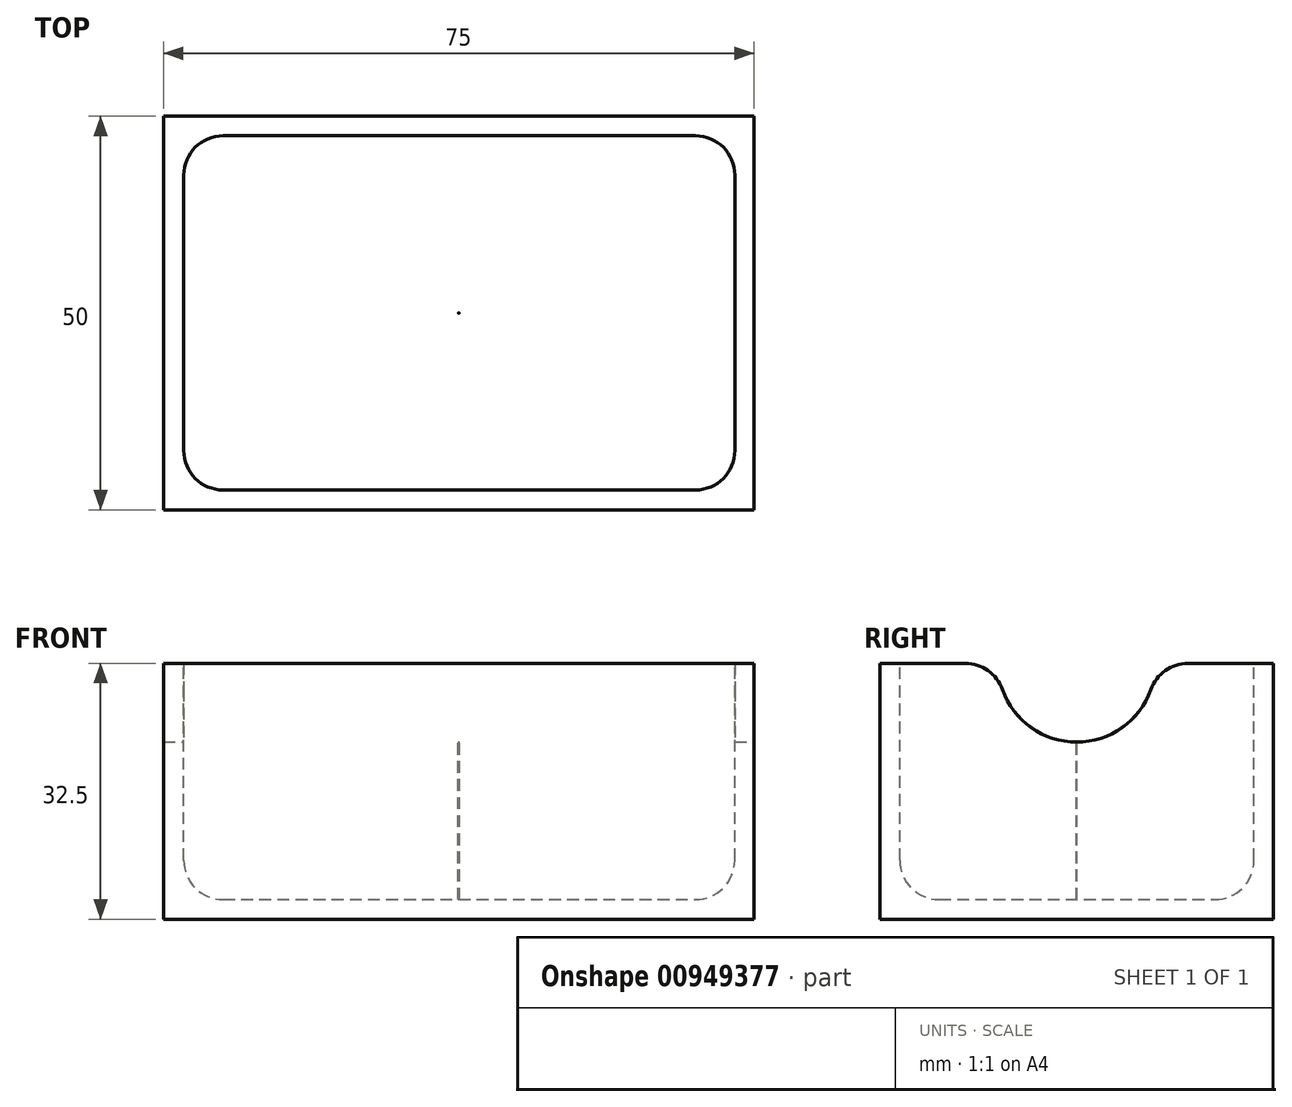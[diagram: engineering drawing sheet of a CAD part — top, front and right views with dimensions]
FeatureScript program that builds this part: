
annotation { "Feature Type Name" : "Feature", "Feature Type Description" : "" }
export const myFeature = defineFeature(function(context is Context, id is Id, definition is map)
    precondition{}
    {
        {
            assignVariable(context, id + "F0", {"name" : "Length", "anyValue" : 75});
        }
        {
            var Q0;
            Q0=qCreatedBy(makeId("Top.planeOp"),FACE);
            var sketch = newSketch(context, id + "F1", { "sketchPlane" : qUnion([Q0])});
            skLineSegment(sketch, "E0.bottom", {"start": v(37.5, -25) * mm, "end": v(-37.5, -25) * mm});
            skLineSegment(sketch, "E0.top", {"start": v(37.5, 25) * mm, "end": v(-37.5, 25) * mm});
            skLineSegment(sketch, "E0.left", {"start": v(37.5, -25) * mm, "end": v(37.5, 25) * mm});
            skLineSegment(sketch, "E0.right", {"start": v(-37.5, -25) * mm, "end": v(-37.5, 25) * mm});
            skPoint(sketch, "E0.middle", {"position": v(0, 0) * mm});
            skSolve(sketch);
        }
        {
            var Q0;
            Q0=makeQuery(id+"F1.imprint","IMPRINT",FACE,{"disambiguationData":[TD([[makeQuery(id+"F1.imprint","IMPRINT",EDGE,{"derivedFrom":sQuery(id+"F1.wireOp",EDGE,"E0.bottom")}),-1.0]])]});
            extrude(context, id + "F2", {"entities" : qUnion([Q0]), "depth" : 32.5 * mm, "offsetDistance" : 25 * mm});
        }
        {
            var Q0;
            Q0=makeQuery(id+"F2.opExtrude","CAP_FACE",FACE,{"disambiguationData":[OSD([sQuery(id+"F1.wireOp",EDGE,"E0.bottom"),sQuery(id+"F1.wireOp",EDGE,"E0.top"),sQuery(id+"F1.wireOp",EDGE,"E0.left"),sQuery(id+"F1.wireOp",EDGE,"E0.right")])],"isStart":false});
            var sketch = newSketch(context, id + "F3", { "sketchPlane" : qUnion([Q0])});
            skLineSegment(sketch, "E1.bottom", {"start": v(-0.07, 0.02) * mm, "end": v(0.07, 0.02) * mm});
            skLineSegment(sketch, "E1.top", {"start": v(-0.07, -0.02) * mm, "end": v(0.07, -0.02) * mm});
            skLineSegment(sketch, "E1.left", {"start": v(-0.07, 0.02) * mm, "end": v(-0.07, -0.02) * mm});
            skLineSegment(sketch, "E1.right", {"start": v(0.07, 0.02) * mm, "end": v(0.07, -0.02) * mm});
            skPoint(sketch, "E1.middle", {"position": v(0, 0) * mm});
            skLineSegment(sketch, "E2.bottom", {"start": v(-34.93, -22.48) * mm, "end": v(35.07, -22.48) * mm});
            skLineSegment(sketch, "E2.top", {"start": v(-34.93, 22.52) * mm, "end": v(35.07, 22.52) * mm});
            skLineSegment(sketch, "E2.left", {"start": v(-34.93, -22.48) * mm, "end": v(-34.93, 22.52) * mm});
            skLineSegment(sketch, "E2.right", {"start": v(35.07, -22.48) * mm, "end": v(35.07, 22.52) * mm});
            skPoint(sketch, "E2.middle", {"position": v(0.07, 0.02) * mm});
            skSolve(sketch);
        }
        {
            var Q0;
            Q0=makeQuery(id+"F3.imprint","IMPRINT",FACE,{"disambiguationData":[TD([[makeQuery(id+"F3.imprint","IMPRINT",EDGE,{"derivedFrom":sQuery(id+"F3.wireOp",EDGE,"E1.bottom")}),1.0]])]});
            extrude(context, id + "F4", {"entities" : qUnion([Q0]), "operationType" : NewBodyOperationType.REMOVE, "oppositeDirection" : true, "depth" : 30 * mm, "offsetDistance" : 25 * mm});
        }
        {
            var Q0;
            Q0=makeQuery(id+"F2.opExtrude","SWEPT_FACE",FACE,{"disambiguationData":[OSD([sQuery(id+"F1.wireOp",EDGE,"E0.left")])]});
            var sketch = newSketch(context, id + "F5", { "sketchPlane" : qUnion([Q0])});
            skCircle(sketch, "E3", {"center": v(0, 32.5) * mm, "radius": 10 * mm});
            skSolve(sketch);
        }
        {
            var Q0;
            Q0 = qSketchRegion(id + "F5", true);
            var Q1;
            {var subQ0=sQuery(id+"F5.wireOp",EDGE,"E3");var subQ1=makeQuery(id+"F2.opExtrude","CAP_EDGE",EDGE,{"disambiguationData":[OSD([sQuery(id+"F1.wireOp",EDGE,"E0.left")])],"isStart":false});var subQ2=makeQuery(id+"F5.imprint","INTERSECT",VERTEX,{"disambiguationData":[OD(0.0)],"derivedFrom":[subQ1,subQ0]});Q1=makeQuery(id+"F5.imprint","IMPRINT",FACE,{"disambiguationData":[TD([[makeQuery(id+"F5.imprint","IMPRINT",EDGE,{"disambiguationData":[TD([[subQ2,-1.0]])],"derivedFrom":subQ0}),1.0]])]});}
            extrude(context, id + "F6", {"entities" : qUnion([Q0, Q1]), "operationType" : NewBodyOperationType.REMOVE, "oppositeDirection" : true, "depth" : (getVariable(context, 'Length') + 1) * mm, "offsetDistance" : 25 * mm});
        }
        {
            var Q0;
            Q0=makeQuery(id+"F4.boolean.opBoolean","COPY",EDGE,{"derivedFrom":makeQuery(id+"F4.opExtrude","SWEPT_EDGE",EDGE,{"disambiguationData":[OSD([sQuery(id+"F3.wireOp",EDGE,"E2.bottom"),sQuery(id+"F3.wireOp",EDGE,"E2.right")])]})});
            var Q1;
            Q1=makeQuery(id+"F4.boolean.opBoolean","COPY",EDGE,{"derivedFrom":makeQuery(id+"F4.opExtrude","CAP_EDGE",EDGE,{"disambiguationData":[OSD([sQuery(id+"F3.wireOp",EDGE,"E2.bottom")])],"isStart":false})});
            var Q2;
            Q2=makeQuery(id+"F4.boolean.opBoolean","COPY",EDGE,{"derivedFrom":makeQuery(id+"F4.opExtrude","CAP_EDGE",EDGE,{"disambiguationData":[OSD([sQuery(id+"F3.wireOp",EDGE,"E2.right")])],"isStart":false})});
            var Q3;
            {var subQ0=sQuery(id+"F1.wireOp",EDGE,"E0.left");var subQ1=sQuery(id+"F1.wireOp",EDGE,"E0.top");var subQ2=sQuery(id+"F1.wireOp",EDGE,"E0.right");var subQ3=sQuery(id+"F1.wireOp",EDGE,"E0.bottom");Q3=makeQuery(id+"F6.boolean.opBoolean","INTERSECT",EDGE,{"disambiguationData":[OD(0.0)],"derivedFrom":[makeQuery(id+"F4.boolean.opBoolean","SPLIT",FACE,{"disambiguationData":[TD([makeQuery(id+"F2.opExtrude","SWEPT_FACE",FACE,{"disambiguationData":[OSD([subQ3])]})])],"derivedFrom":makeQuery(id+"F2.opExtrude","CAP_FACE",FACE,{"disambiguationData":[OSD([subQ3,subQ1,subQ0,subQ2])],"isStart":false})}),makeQuery(id+"F6.opExtrude","SWEPT_FACE",FACE,{"disambiguationData":[OSD([sQuery(id+"F5.wireOp",EDGE,"E3")])]})]});}
            var Q4;
            {var subQ0=sQuery(id+"F1.wireOp",EDGE,"E0.left");var subQ1=sQuery(id+"F1.wireOp",EDGE,"E0.top");var subQ2=sQuery(id+"F1.wireOp",EDGE,"E0.right");var subQ3=sQuery(id+"F1.wireOp",EDGE,"E0.bottom");Q4=makeQuery(id+"F6.boolean.opBoolean","INTERSECT",EDGE,{"disambiguationData":[OD(2.0)],"derivedFrom":[makeQuery(id+"F4.boolean.opBoolean","SPLIT",FACE,{"disambiguationData":[TD([makeQuery(id+"F2.opExtrude","SWEPT_FACE",FACE,{"disambiguationData":[OSD([subQ3])]})])],"derivedFrom":makeQuery(id+"F2.opExtrude","CAP_FACE",FACE,{"disambiguationData":[OSD([subQ3,subQ1,subQ0,subQ2])],"isStart":false})}),makeQuery(id+"F6.opExtrude","SWEPT_FACE",FACE,{"disambiguationData":[OSD([sQuery(id+"F5.wireOp",EDGE,"E3")])]})]});}
            var Q5;
            {var subQ0=sQuery(id+"F1.wireOp",EDGE,"E0.left");var subQ1=sQuery(id+"F1.wireOp",EDGE,"E0.top");var subQ2=sQuery(id+"F1.wireOp",EDGE,"E0.right");var subQ3=sQuery(id+"F1.wireOp",EDGE,"E0.bottom");Q5=makeQuery(id+"F6.boolean.opBoolean","INTERSECT",EDGE,{"disambiguationData":[OD(3.0)],"derivedFrom":[makeQuery(id+"F4.boolean.opBoolean","SPLIT",FACE,{"disambiguationData":[TD([makeQuery(id+"F2.opExtrude","SWEPT_FACE",FACE,{"disambiguationData":[OSD([subQ3])]})])],"derivedFrom":makeQuery(id+"F2.opExtrude","CAP_FACE",FACE,{"disambiguationData":[OSD([subQ3,subQ1,subQ0,subQ2])],"isStart":false})}),makeQuery(id+"F6.opExtrude","SWEPT_FACE",FACE,{"disambiguationData":[OSD([sQuery(id+"F5.wireOp",EDGE,"E3")])]})]});}
            var Q6;
            {var subQ0=sQuery(id+"F1.wireOp",EDGE,"E0.left");var subQ1=sQuery(id+"F1.wireOp",EDGE,"E0.top");var subQ2=sQuery(id+"F1.wireOp",EDGE,"E0.right");var subQ3=sQuery(id+"F1.wireOp",EDGE,"E0.bottom");Q6=makeQuery(id+"F6.boolean.opBoolean","INTERSECT",EDGE,{"disambiguationData":[OD(1.0)],"derivedFrom":[makeQuery(id+"F4.boolean.opBoolean","SPLIT",FACE,{"disambiguationData":[TD([makeQuery(id+"F2.opExtrude","SWEPT_FACE",FACE,{"disambiguationData":[OSD([subQ3])]})])],"derivedFrom":makeQuery(id+"F2.opExtrude","CAP_FACE",FACE,{"disambiguationData":[OSD([subQ3,subQ1,subQ0,subQ2])],"isStart":false})}),makeQuery(id+"F6.opExtrude","SWEPT_FACE",FACE,{"disambiguationData":[OSD([sQuery(id+"F5.wireOp",EDGE,"E3")])]})]});}
            var Q7;
            Q7=makeQuery(id+"F4.boolean.opBoolean","COPY",EDGE,{"derivedFrom":makeQuery(id+"F4.opExtrude","SWEPT_EDGE",EDGE,{"disambiguationData":[OSD([sQuery(id+"F3.wireOp",EDGE,"E2.top"),sQuery(id+"F3.wireOp",EDGE,"E2.right")])]})});
            var Q8;
            Q8=makeQuery(id+"F4.boolean.opBoolean","COPY",EDGE,{"derivedFrom":makeQuery(id+"F4.opExtrude","CAP_EDGE",EDGE,{"disambiguationData":[OSD([sQuery(id+"F3.wireOp",EDGE,"E2.top")])],"isStart":false})});
            var Q9;
            Q9=makeQuery(id+"F4.boolean.opBoolean","COPY",EDGE,{"derivedFrom":makeQuery(id+"F4.opExtrude","CAP_EDGE",EDGE,{"disambiguationData":[OSD([sQuery(id+"F3.wireOp",EDGE,"E2.left")])],"isStart":false})});
            var Q10;
            Q10=makeQuery(id+"F4.boolean.opBoolean","COPY",EDGE,{"derivedFrom":makeQuery(id+"F4.opExtrude","SWEPT_EDGE",EDGE,{"disambiguationData":[OSD([sQuery(id+"F3.wireOp",EDGE,"E2.bottom"),sQuery(id+"F3.wireOp",EDGE,"E2.left")])]})});
            var Q11;
            Q11=makeQuery(id+"F4.boolean.opBoolean","COPY",EDGE,{"derivedFrom":makeQuery(id+"F4.opExtrude","SWEPT_EDGE",EDGE,{"disambiguationData":[OSD([sQuery(id+"F3.wireOp",EDGE,"E2.top"),sQuery(id+"F3.wireOp",EDGE,"E2.left")])]})});
            fillet(context, id + "F7", {"entities" : qUnion([Q0, Q1, Q2, Q3, Q4, Q5, Q6, Q7, Q8, Q9, Q10, Q11]), "radius" : 5 * mm, "tangentPropagation" : true, "allowEdgeOverflow" : false});
        }
    });
